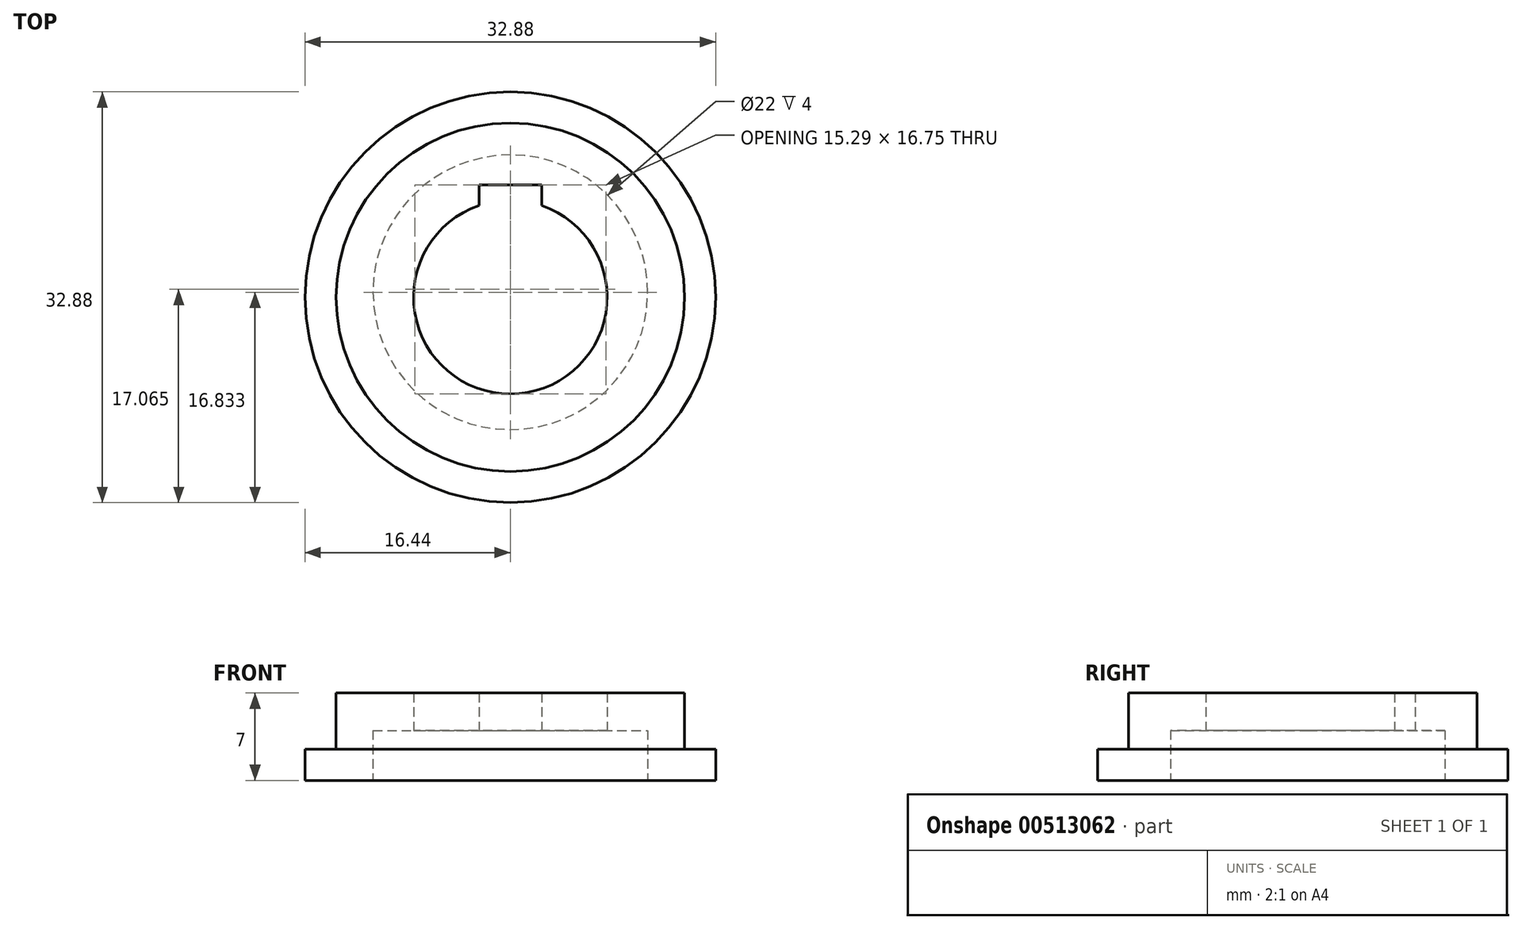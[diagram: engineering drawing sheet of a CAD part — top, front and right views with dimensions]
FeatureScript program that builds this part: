
annotation { "Feature Type Name" : "Feature", "Feature Type Description" : "" }
export const myFeature = defineFeature(function(context is Context, id is Id, definition is map)
    precondition{}
    {
        {
            var Q0;
            Q0=qCreatedBy(makeId("Top.planeOp"),FACE);
            var sketch = newSketch(context, id + "F0", { "sketchPlane" : qUnion([Q0])});
            skCircle(sketch, "E0", {"center": v(0, 0) * mm, "radius": 13.95 * mm});
            skSolve(sketch);
        }
        {
            var Q0;
            Q0=makeQuery(id+"F0.imprint","IMPRINT",FACE,{"disambiguationData":[TD([[makeQuery(id+"F0.imprint","IMPRINT",EDGE,{"derivedFrom":sQuery(id+"F0.wireOp",EDGE,"E0")}),1.0]])]});
            extrude(context, id + "F1", {"entities" : qUnion([Q0]), "depth" : 7 * mm});
        }
        {
            var Q0;
            Q0=makeQuery(id+"F1.opExtrude","CAP_FACE",FACE,{"disambiguationData":[OSD([sQuery(id+"F0.wireOp",EDGE,"E0")])],"isStart":true});
            var sketch = newSketch(context, id + "F2", { "sketchPlane" : qUnion([Q0])});
            skCircle(sketch, "E1", {"center": v(0, -0.4) * mm, "radius": 11 * mm});
            skSolve(sketch);
        }
        {
            var Q0;
            Q0=makeQuery(id+"F2.imprint","IMPRINT",FACE,{"disambiguationData":[TD([[makeQuery(id+"F2.imprint","IMPRINT",EDGE,{"derivedFrom":sQuery(id+"F2.wireOp",EDGE,"E1")}),1.0]])]});
            extrude(context, id + "F3", {"entities" : qUnion([Q0]), "operationType" : NewBodyOperationType.REMOVE, "oppositeDirection" : true, "depth" : 4 * mm});
        }
        {
            var Q0;
            Q0=makeQuery(id+"F3.boolean.opBoolean","COPY",FACE,{"derivedFrom":makeQuery(id+"F3.opExtrude","CAP_FACE",FACE,{"disambiguationData":[OSD([sQuery(id+"F2.wireOp",EDGE,"E1")])],"isStart":false})});
            var sketch = newSketch(context, id + "F4", { "sketchPlane" : qUnion([Q0])});
            skCircle(sketch, "E2", {"center": v(0, 0) * mm, "radius": 7.75 * mm});
            skSolve(sketch);
        }
        {
            var Q0;
            Q0=makeQuery(id+"F4.imprint","IMPRINT",FACE,{"disambiguationData":[TD([[makeQuery(id+"F4.imprint","IMPRINT",EDGE,{"derivedFrom":sQuery(id+"F4.wireOp",EDGE,"E2")}),1.0]])]});
            extrude(context, id + "F5", {"entities" : qUnion([Q0]), "operationType" : NewBodyOperationType.REMOVE, "oppositeDirection" : true, "depth" : 25 * mm});
        }
        {
            var Q0;
            Q0=qCreatedBy(makeId("Front.planeOp"),FACE);
            var sketch = newSketch(context, id + "F6", { "sketchPlane" : qUnion([Q0])});
            skLineSegment(sketch, "E3", {"start": v(16.44, 0) * mm, "end": v(16.44, 2.5) * mm});
            skLineSegment(sketch, "E4", {"start": v(16.44, 2.5) * mm, "end": v(13.94, 2.5) * mm});
            skLineSegment(sketch, "E5", {"start": v(13.94, 2.5) * mm, "end": v(13.94, 0) * mm});
            skLineSegment(sketch, "E6", {"start": v(0, 0) * mm, "end": v(0, 10.4) * mm});
            skLineSegment(sketch, "E7", {"start": v(13.94, 0) * mm, "end": v(16.44, 0) * mm});
            skSolve(sketch);
        }
        {
            var Q0;
            Q0=makeQuery(id+"F6.imprint","IMPRINT",FACE,{"disambiguationData":[TD([[makeQuery(id+"F6.imprint","IMPRINT",EDGE,{"derivedFrom":sQuery(id+"F6.wireOp",EDGE,"E3")}),1.0]])]});
            var Q1;
            Q1=sQuery(id+"F6.wireOp",EDGE,"E6");
            revolve(context, id + "F7", {"operationType" : NewBodyOperationType.ADD, "entities" : qUnion([Q0]), "axis" : qUnion([Q1]), "revolveType" : RevolveType.FULL});
        }
        {
            var Q0;
            Q0=qCreatedBy(makeId("Top.planeOp"),FACE);
            var sketch = newSketch(context, id + "F8", { "sketchPlane" : qUnion([Q0])});
            skLineSegment(sketch, "E8", {"start": v(-2.5, 0) * mm, "end": v(-2.5, 9) * mm});
            skLineSegment(sketch, "E9", {"start": v(-2.5, 9) * mm, "end": v(2.5, 9) * mm});
            skLineSegment(sketch, "E10", {"start": v(2.5, 9) * mm, "end": v(2.5, 0) * mm});
            skLineSegment(sketch, "E11", {"start": v(2.5, 0) * mm, "end": v(-2.5, 0) * mm});
            skSolve(sketch);
        }
        {
            var Q0;
            Q0=makeQuery(id+"F8.imprint","IMPRINT",FACE,{"disambiguationData":[TD([[makeQuery(id+"F8.imprint","IMPRINT",EDGE,{"derivedFrom":sQuery(id+"F8.wireOp",EDGE,"E8")}),-1.0]])]});
            extrude(context, id + "F9", {"entities" : qUnion([Q0]), "operationType" : NewBodyOperationType.REMOVE, "depth" : 25 * mm});
        }
    });
